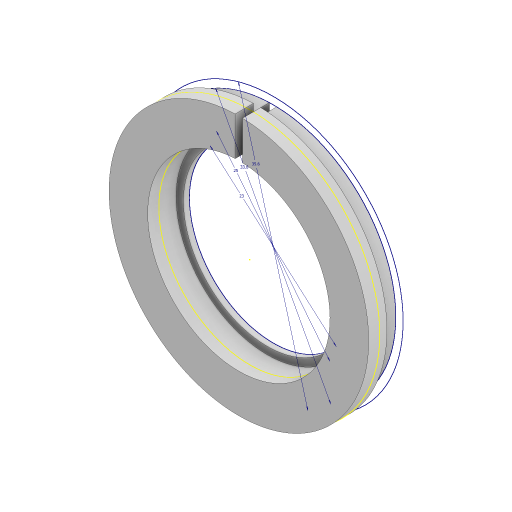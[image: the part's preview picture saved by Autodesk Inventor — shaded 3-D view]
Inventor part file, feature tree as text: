
AUTODESK INVENTOR PART (.ipt)
format: ipt  version: 2023 (Build 270158000, 158)  size: 159,744 bytes
history: native  units: mm
features: extrude x5, sketch x3
ambient origin geometry x8: Origin, YZ Plane, XZ Plane, XY Plane, X Axis, Y Axis, Z Axis, Center Point
bodies: Solid1 (feature_tree)
feature tree (8):
  sketch  "Sketch1"  dims[d0=33.6mm d1=23.0mm]
  extrude  "Extrusion1"  Depth=23.0mm
  extrude  "Extrusion2"  Depth=25.0mm
  sketch  "Sketch2"  dims[d2=35.6mm d3=25.0mm]
  extrude  "Extrusion3"  Depth=3.2mm TaperAngle=0.0deg
  extrude  "Extrusion5"  Depth=1.0mm TaperAngle=0.0deg
  extrude  "Extrusion4"  Depth=1.0mm
  sketch  "Sketch3"  dims[d4=0.8mm d5=0.0mm d6=3.2mm d7=0.0mm d8=1.5mm d9=0.0mm d10=1.0mm d11=16.0mm d12=10.0mm d13=0.0mm d14=1.0mm d15=0.0mm d16=0.5mm d17=0.872665mm d18=0.5mm d19=0.872665mm]
